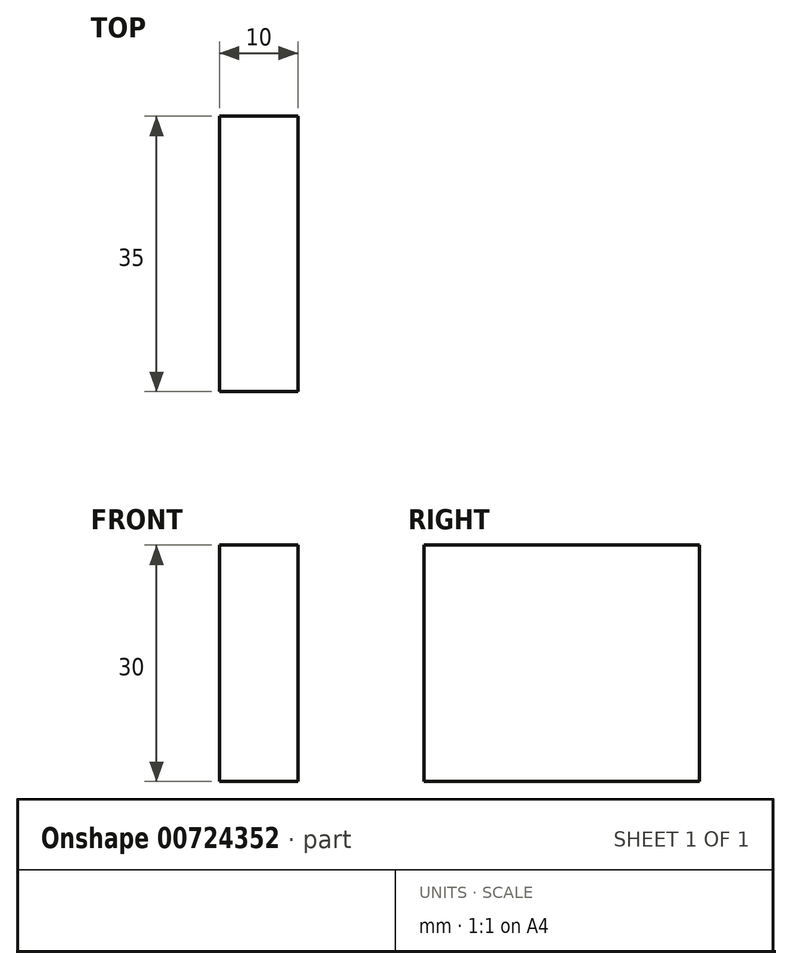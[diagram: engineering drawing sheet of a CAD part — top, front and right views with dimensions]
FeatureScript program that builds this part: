
annotation { "Feature Type Name" : "Feature", "Feature Type Description" : "" }
export const myFeature = defineFeature(function(context is Context, id is Id, definition is map)
    precondition{}
    {
        {
            var Q0;
            Q0=qCreatedBy(makeId("Front.planeOp"),FACE);
            var sketch = newSketch(context, id + "F0", { "sketchPlane" : qUnion([Q0])});
            skLineSegment(sketch, "E0.bottom", {"start": v(0, 0) * mm, "end": v(-10, 0) * mm});
            skLineSegment(sketch, "E0.top", {"start": v(0, 30) * mm, "end": v(-10, 30) * mm});
            skLineSegment(sketch, "E0.left", {"start": v(0, 0) * mm, "end": v(0, 30) * mm});
            skLineSegment(sketch, "E0.right", {"start": v(-10, 0) * mm, "end": v(-10, 30) * mm});
            skSolve(sketch);
        }
        {
            var Q0;
            Q0=makeQuery(id+"F0.imprint","IMPRINT",FACE,{"disambiguationData":[TD([[makeQuery(id+"F0.imprint","IMPRINT",EDGE,{"derivedFrom":sQuery(id+"F0.wireOp",EDGE,"E0.bottom")}),-1.0]])]});
            extrude(context, id + "F1", {"entities" : qUnion([Q0]), "depth" : 35 * mm, "offsetDistance" : 25 * mm});
        }
    });
